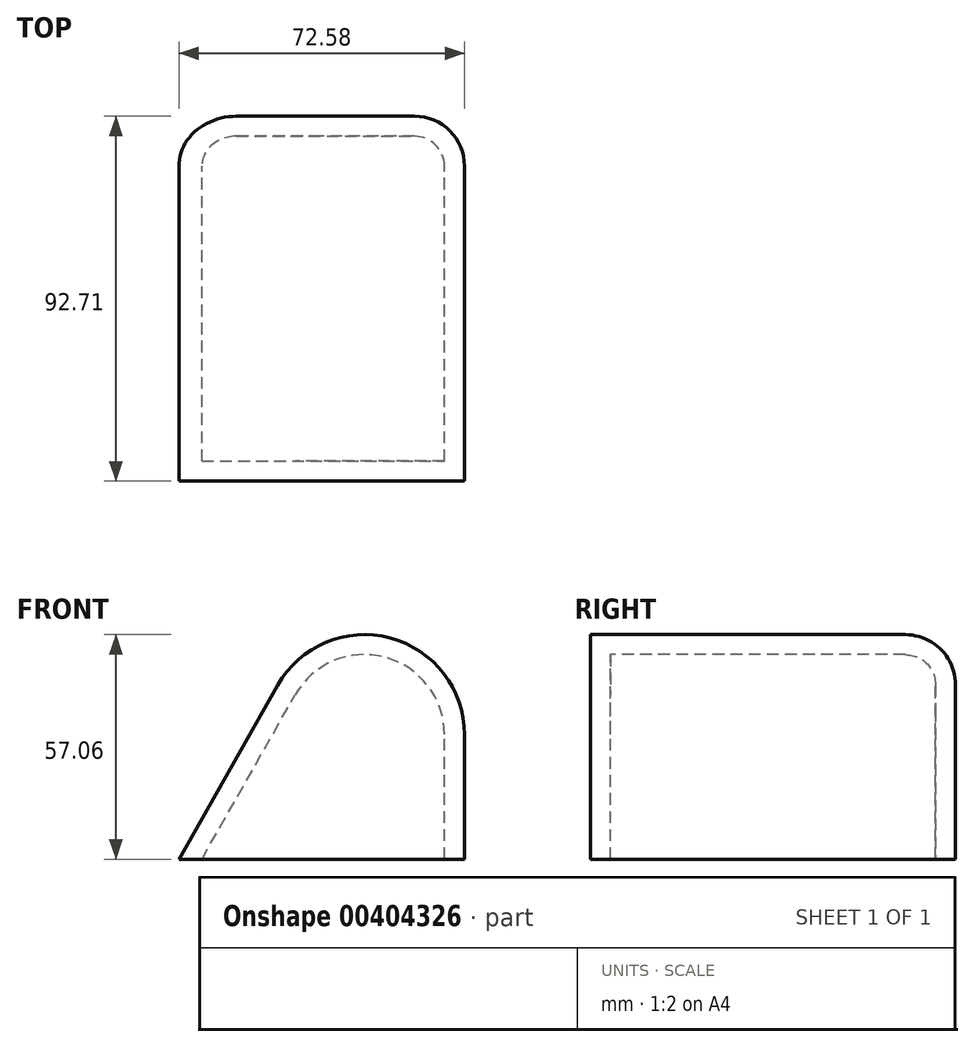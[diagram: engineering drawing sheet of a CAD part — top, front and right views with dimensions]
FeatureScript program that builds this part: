
annotation { "Feature Type Name" : "Feature", "Feature Type Description" : "" }
export const myFeature = defineFeature(function(context is Context, id is Id, definition is map)
    precondition{}
    {
        {
            var Q0;
            Q0=qCreatedBy(makeId("Front.planeOp"),FACE);
            var sketch = newSketch(context, id + "F0", { "sketchPlane" : qUnion([Q0])});
            skLineSegment(sketch, "E0", {"start": v(0, 0) * mm, "end": v(72.58, 0) * mm});
            skLineSegment(sketch, "E1", {"start": v(72.58, 0) * mm, "end": v(72.58, 127.86) * mm});
            skLineSegment(sketch, "E2", {"start": v(0, 0) * mm, "end": v(72.58, 127.86) * mm});
            skSolve(sketch);
        }
        {
            var Q0;
            Q0=makeQuery(id+"F0.imprint","IMPRINT",FACE,{"disambiguationData":[TD([[makeQuery(id+"F0.imprint","IMPRINT",EDGE,{"derivedFrom":sQuery(id+"F0.wireOp",EDGE,"E0")}),1.0]])]});
            extrude(context, id + "F1", {"entities" : qUnion([Q0]), "depth" : 92.7 * mm});
        }
        {
            var Q0;
            Q0=makeQuery(id+"F1.opExtrude","SWEPT_EDGE",EDGE,{"disambiguationData":[OSD([sQuery(id+"F0.wireOp",EDGE,"E1"),sQuery(id+"F0.wireOp",EDGE,"E2")])]});
            fillet(context, id + "F2", {"entities" : qUnion([Q0]), "radius" : 25.4 * mm, "tangentPropagation" : true, "allowEdgeOverflow" : false});
        }
        {
            var Q0;
            {var subQ0=sQuery(id+"F0.wireOp",EDGE,"E2");var subQ1=sQuery(id+"F0.wireOp",EDGE,"E1");Q0=makeQuery(id+"F2.opFillet","BLEND_EDGE",EDGE,{"blendedFrom":[makeQuery(id+"F1.opExtrude","SWEPT_EDGE",EDGE,{"disambiguationData":[OSD([subQ1,subQ0])]}),makeQuery(id+"F1.opExtrude","CAP_FACE",FACE,{"disambiguationData":[OSD([sQuery(id+"F0.wireOp",EDGE,"E0"),subQ1,subQ0])],"isStart":true})],"blendedInto":[makeQuery(id+"F1.opExtrude","CAP_FACE",FACE,{"disambiguationData":[OSD([sQuery(id+"F0.wireOp",EDGE,"E0"),subQ1,subQ0])],"isStart":true})]});}
            fillet(context, id + "F3", {"entities" : qUnion([Q0]), "radius" : 12.7 * mm, "tangentPropagation" : true, "allowEdgeOverflow" : false});
        }
        {
            var Q0;
            Q0=makeQuery(id+"F1.opExtrude","SWEPT_FACE",FACE,{"disambiguationData":[OSD([sQuery(id+"F0.wireOp",EDGE,"E0")])]});
            shell(context, id + "F4", {"entities" : qUnion([Q0]), "thickness" : 5.08 * mm});
        }
    });
